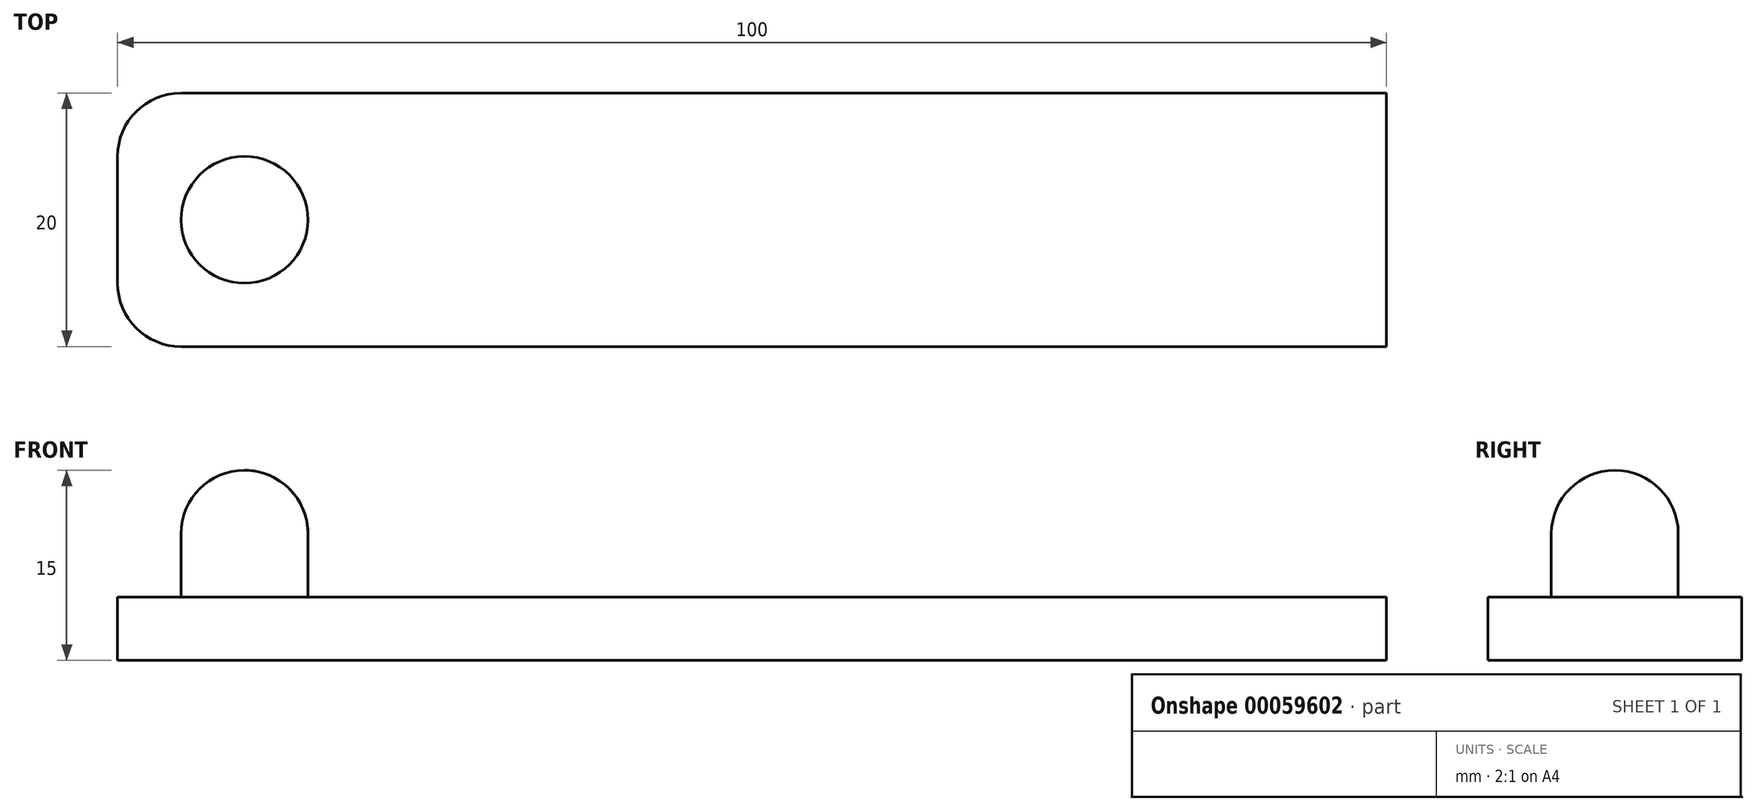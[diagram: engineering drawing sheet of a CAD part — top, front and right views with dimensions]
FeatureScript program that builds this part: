
annotation { "Feature Type Name" : "Feature", "Feature Type Description" : "" }
export const myFeature = defineFeature(function(context is Context, id is Id, definition is map)
    precondition{}
    {
        {
            var Q0;
            Q0=qCreatedBy(makeId("Top.planeOp"),FACE);
            var sketch = newSketch(context, id + "F0", { "sketchPlane" : qUnion([Q0])});
            skLineSegment(sketch, "E0.bottom", {"start": v(-10, 10) * mm, "end": v(90, 10) * mm});
            skLineSegment(sketch, "E0.top", {"start": v(-10, -10) * mm, "end": v(90, -10) * mm});
            skLineSegment(sketch, "E0.left", {"start": v(-10, 10) * mm, "end": v(-10, -10) * mm});
            skLineSegment(sketch, "E0.right", {"start": v(90, 10) * mm, "end": v(90, -10) * mm});
            skSolve(sketch);
        }
        {
            var Q0;
            Q0 = qSketchRegion(id + "F0", true);
            extrude(context, id + "F1", {"entities" : qUnion([Q0]), "depth" : 5 * mm});
        }
        {
            var Q0;
            Q0=makeQuery(id+"F1.opExtrude","CAP_FACE",FACE,{"disambiguationData":[OSD([sQuery(id+"F0.wireOp",EDGE,"E0.bottom"),sQuery(id+"F0.wireOp",EDGE,"E0.top"),sQuery(id+"F0.wireOp",EDGE,"E0.left"),sQuery(id+"F0.wireOp",EDGE,"E0.right")])],"isStart":false});
            var sketch = newSketch(context, id + "F2", { "sketchPlane" : qUnion([Q0])});
            skCircle(sketch, "E1", {"center": v(0, 0) * mm, "radius": 5 * mm});
            skSolve(sketch);
        }
        {
            var Q0;
            Q0 = qSketchRegion(id + "F2", true);
            extrude(context, id + "F3", {"entities" : qUnion([Q0]), "operationType" : NewBodyOperationType.ADD, "depth" : 10 * mm});
        }
        {
            var Q0;
            Q0=makeQuery(id+"F1.opExtrude","SWEPT_EDGE",EDGE,{"disambiguationData":[OSD([sQuery(id+"F0.wireOp",EDGE,"E0.top"),sQuery(id+"F0.wireOp",EDGE,"E0.left")])]});
            var Q1;
            Q1=makeQuery(id+"F1.opExtrude","SWEPT_EDGE",EDGE,{"disambiguationData":[OSD([sQuery(id+"F0.wireOp",EDGE,"E0.bottom"),sQuery(id+"F0.wireOp",EDGE,"E0.left")])]});
            fillet(context, id + "F4", {"entities" : qUnion([Q0, Q1]), "radius" : 5 * mm, "tangentPropagation" : true, "allowEdgeOverflow" : false});
        }
        {
            var Q0;
            Q0=makeQuery(id+"F3.opExtrude","CAP_EDGE",EDGE,{"disambiguationData":[OSD([sQuery(id+"F2.wireOp",EDGE,"E1")])],"isStart":false});
            fillet(context, id + "F5", {"entities" : qUnion([Q0]), "radius" : 5 * mm, "tangentPropagation" : true, "allowEdgeOverflow" : false});
        }
    });
